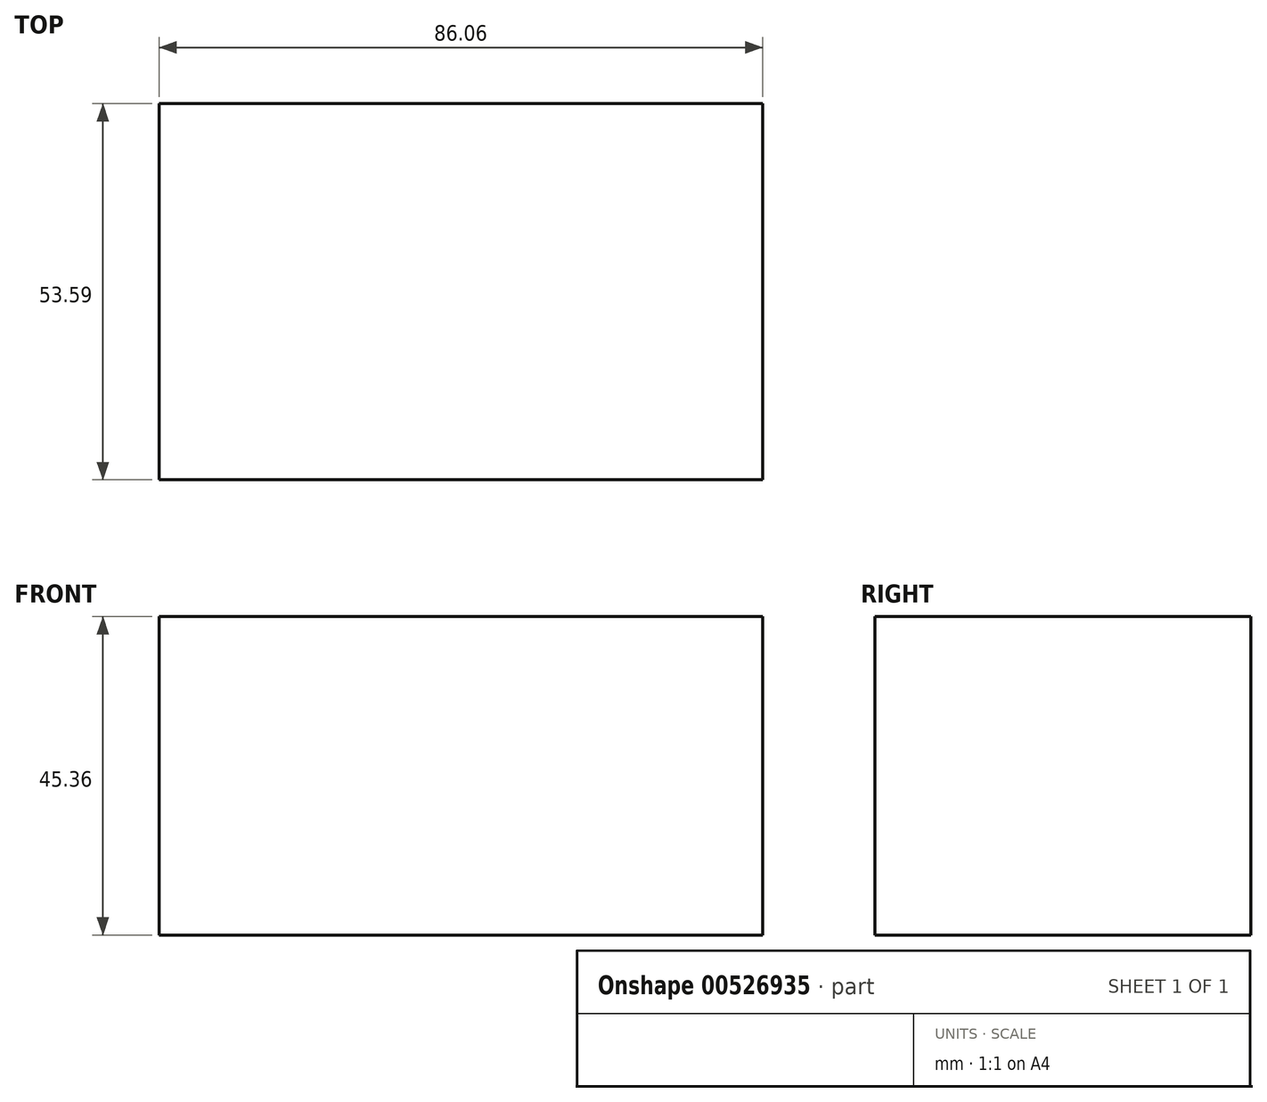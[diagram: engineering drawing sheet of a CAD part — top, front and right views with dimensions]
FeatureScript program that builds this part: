
annotation { "Feature Type Name" : "Feature", "Feature Type Description" : "" }
export const myFeature = defineFeature(function(context is Context, id is Id, definition is map)
    precondition{}
    {
        {
            var Q0;
            Q0=qCreatedBy(makeId("Front.planeOp"),FACE);
            var sketch = newSketch(context, id + "F0", { "sketchPlane" : qUnion([Q0])});
            skLineSegment(sketch, "E0.bottom", {"start": v(-22.56, -19.54) * mm, "end": v(63.5, -19.54) * mm});
            skLineSegment(sketch, "E0.top", {"start": v(-22.56, 25.82) * mm, "end": v(63.5, 25.82) * mm});
            skLineSegment(sketch, "E0.left", {"start": v(-22.56, -19.54) * mm, "end": v(-22.56, 25.82) * mm});
            skLineSegment(sketch, "E0.right", {"start": v(63.5, -19.54) * mm, "end": v(63.5, 25.82) * mm});
            skSolve(sketch);
        }
        {
            var Q0;
            Q0 = qSketchRegion(id + "F0", true);
            extrude(context, id + "F1", {"entities" : qUnion([Q0]), "depth" : 53.6 * mm, "offsetDistance" : 25.4 * mm});
        }
    });
